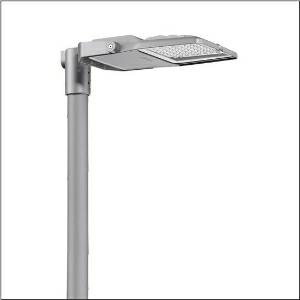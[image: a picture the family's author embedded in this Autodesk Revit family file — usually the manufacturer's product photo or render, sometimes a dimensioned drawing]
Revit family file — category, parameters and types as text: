
# Revit family: floodlight_fl_21_mini___pl43_5xa7771d4a3a_ee73
name_source: partatom
category: Lighting Fixtures
units: mm (PartAtom-declared; Revit-internal decimal feet)

## family parameters
Cut with Voids When Loaded = No
Host = Face
Light Source = No
Part Type = Normal
Room Calculation Point = No
Round Connector Dimension = Use Diameter
Shared = No

## types (1)
- --- (1 x LED, 19090 lm, 143 W, 4000K)
    Apparent Load = 143 VA
    CIE Flux Codes = 27 78 99 100 100
    Color Rendering = 70
    Color Temperature = 4000K
    Default Elevation = 1800 mm
    Description = Floodlight FL 21 mini, floodlight, primary light control with lens, of PMMA, primary optical cover: protective disc, of toughened safety glass, transparent, light distribution: PL43, light emission: direct distribution, installation type: surface-mounted, LED, High Power LED, rated luminous flux: 19.090lm, luminous efficacy: 133lm/W, light colour: 740, colour temperature: 4000K, control gear: ECG iQ, control: Auto-Match, Temp-Guard, Lumen-Switch, Night-Set, Smart-Wire, Light-Fading, Desk-Remote (wireless, voltage-free reading and setting of iQ features in the workshop via application-optimized NFC function/RFID function), optimised constant luminous flux control (CLO 2.0), with terminal, 6-pole, mains connection: 220..240V, AC, 50/60Hz, start of lifetime: 143W, end of lifetime: 152W, reduction: 61W, luminaire housing, of diecast aluminium, powder-coated, Siteco® metallic grey (DB 702S), corrosivity category C5 according to DIN EN ISO 12944, mast bracket, of steel, galvanised, powder-coated, Siteco® metallic grey (DB 702S), protection rating (complete): IP66, insulation class (complete): insulation class II (safety insulation), certification: CE, ENEC, VDE, protection symbol: D, impact resistance: IK08, permissible operating ambient temperature: -40..+40°C, permissible operating ambient temperature for outdoor applications: -40..+50°C, standard: DIN EN 12944, packaging unit: 1 piece

Light Distribution: PL43
    Height = 70 mm
    Lamp = 1 x LED
    Lamp Light Flux = 19090 lm
    Lamp Power = 143 W
    Lamp count = 1
    Length = 485 mm
    Luminous efficacy = 133 lm/W
    Manufacturer = Siteco
    ModVariant = No
    Model = 5XA7771D4A3A
    Number of Poles = 1
    OnlyDefault = Yes
    Power Factor = 1
    Product Name = Floodlight FL 21 mini | PL43
    Product group = floodlight | pylon top
    ProductGroupID = 6101
    Protection Class = Protection class II
    Protection Degree = IP 66
    RLX_Detail_Level = 1
    RlxData = <blob elided: 101337 chars, md5=f15278b6>
    Socket = socket
    Standby Power = 0 W
    System Light Flux = 19090 lm
    System Power = 143 W
    Type Comments = factory setting: luminous flux: 100 % | dim-lin: 254 | 730 mA
    Type Image = l_1007125.jpg
    URL = http://relux.com
    VarID = @adj_072941
    Voltage = 0 V
    Weight = 0.00 kg
    Width = 337 mm

## geometry (parser evidence)
native form markers: Blend x4, Sweep x10
no freeform markers — native parametric forms only
